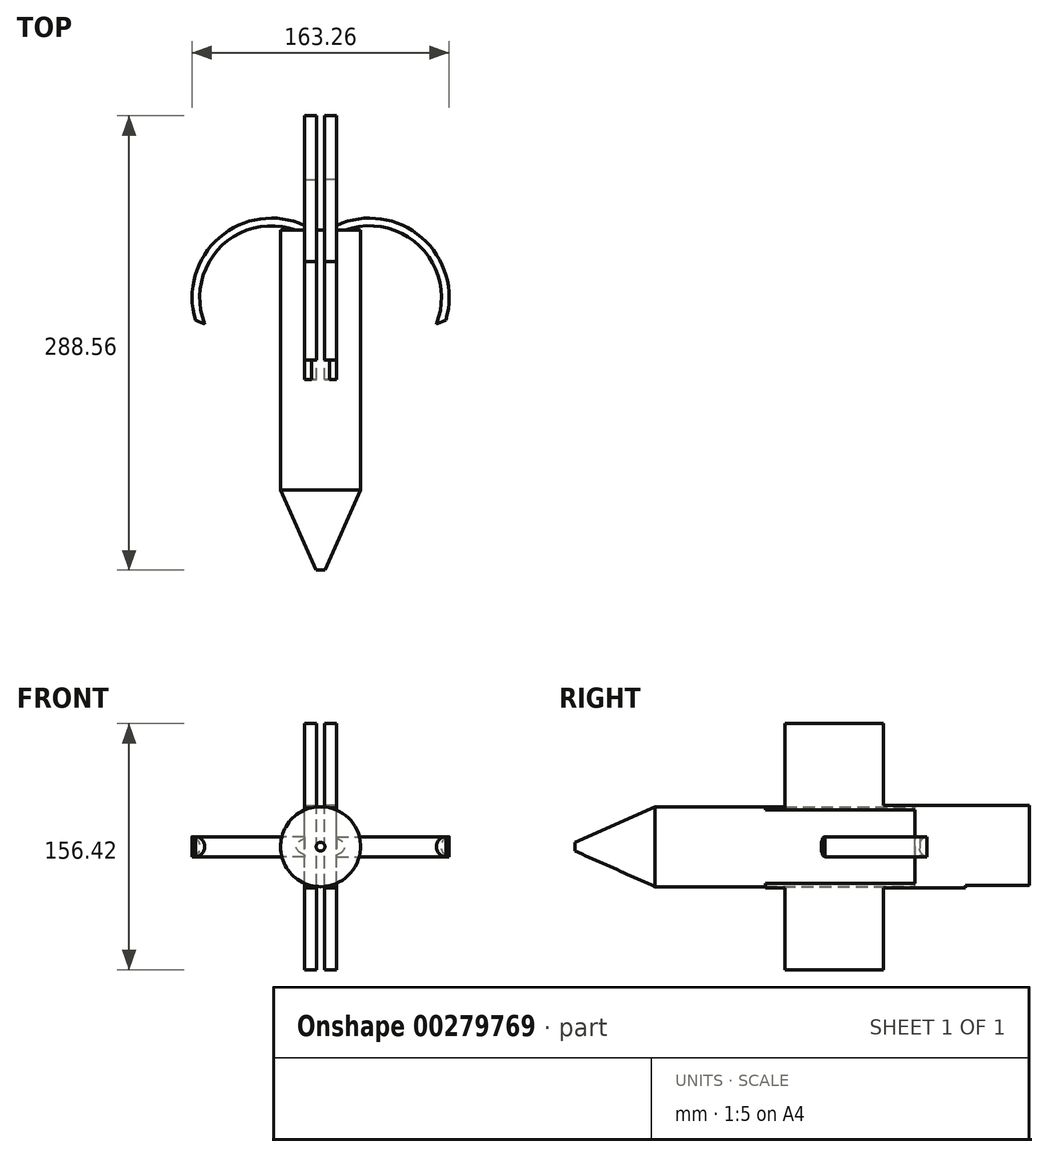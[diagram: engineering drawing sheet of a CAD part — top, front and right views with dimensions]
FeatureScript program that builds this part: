
annotation { "Feature Type Name" : "Feature", "Feature Type Description" : "" }
export const myFeature = defineFeature(function(context is Context, id is Id, definition is map)
    precondition{}
    {
        {
            var Q0;
            Q0=qCreatedBy(makeId("Top.planeOp"),FACE);
            var sketch = newSketch(context, id + "F0", { "sketchPlane" : qUnion([Q0])});
            skLineSegment(sketch, "E0.bottom", {"start": v(-10.87, 76.2) * mm, "end": v(13.75, 76.2) * mm});
            skLineSegment(sketch, "E0.top", {"start": v(-10.87, -76.2) * mm, "end": v(13.75, -76.2) * mm});
            skLineSegment(sketch, "E0.left", {"start": v(-10.87, 76.2) * mm, "end": v(-10.87, -76.2) * mm});
            skLineSegment(sketch, "E0.right", {"start": v(13.75, 76.2) * mm, "end": v(13.75, -76.2) * mm});
            skSolve(sketch);
        }
        {
            var Q0;
            Q0=makeQuery(id+"F0.imprint","IMPRINT",FACE,{"disambiguationData":[TD([[makeQuery(id+"F0.imprint","IMPRINT",EDGE,{"derivedFrom":sQuery(id+"F0.wireOp",EDGE,"E0.bottom")}),-1.0]])]});
            var Q1;
            Q1=sQuery(id+"F0.wireOp",EDGE,"E0.right");
            revolve(context, id + "F1", {"entities" : qUnion([Q0]), "axis" : qUnion([Q1]), "revolveType" : RevolveType.FULL});
        }
        {
            var Q0;
            Q0=makeQuery(id+"F1.opRevolve","SWEPT_BODY",BODY,{"disambiguationData":[OSD([sQuery(id+"F0.wireOp",EDGE,"E0.bottom"),sQuery(id+"F0.wireOp",EDGE,"E0.top"),sQuery(id+"F0.wireOp",EDGE,"E0.left"),sQuery(id+"F0.wireOp",EDGE,"E0.right")])]});
            deleteBodies(context, id + "F2", {"entities" : qUnion([Q0])});
        }
        {
            var Q0;
            Q0=qCreatedBy(makeId("Front.planeOp"),FACE);
            var sketch = newSketch(context, id + "F3", { "sketchPlane" : qUnion([Q0])});
            skCircle(sketch, "E1", {"center": v(0, 0) * mm, "radius": 25.4 * mm});
            skSolve(sketch);
        }
        {
            var Q0;
            Q0=makeQuery(id+"F3.imprint","IMPRINT",FACE,{"disambiguationData":[TD([[makeQuery(id+"F3.imprint","IMPRINT",EDGE,{"derivedFrom":sQuery(id+"F3.wireOp",EDGE,"E1")}),1.0]])]});
            extrude(context, id + "F4", {"entities" : qUnion([Q0]), "endBound" : BoundingType.SYMMETRIC, "depth" : 165.1 * mm});
        }
        {
            var Q0;
            Q0=qCreatedBy(makeId("Right.planeOp"),FACE);
            cPlane(context, id + "F5", {"entities" : qUnion([Q0]), "cplaneType" : CPlaneType.OFFSET, "offset" : 2.54 * mm, "width" : 152.4 * mm, "height" : 152.4 * mm});
        }
        {
            var Q0;
            Q0=makeQuery(id+"F4.opExtrude","CAP_FACE",FACE,{"disambiguationData":[OSD([sQuery(id+"F3.wireOp",EDGE,"E1")])],"isStart":false});
            var sketch = newSketch(context, id + "F6", { "sketchPlane" : qUnion([Q0])});
            skLineSegment(sketch, "E2", {"start": v(0, -2.99) * mm, "end": v(25.36, -1.5) * mm});
            skPoint(sketch, "E3", {"position": v(-28.9, -49.12) * mm});
            skPoint(sketch, "E4", {"position": v(0, -2.99) * mm});
            skPoint(sketch, "E5", {"position": v(-47.51, -18.61) * mm});
            skSolve(sketch);
        }
        {
            var Q0;
            Q0=qCreatedBy(makeId("Right.planeOp"),FACE);
            cPlane(context, id + "F7", {"entities" : qUnion([Q0]), "cplaneType" : CPlaneType.OFFSET, "offset" : 25.4 * mm, "width" : 152.4 * mm, "height" : 152.4 * mm});
        }
        {
            var Q0;
            Q0=qCreatedBy(id+"F5.planeOp",FACE);
            var sketch = newSketch(context, id + "F8", { "sketchPlane" : qUnion([Q0])});
            skLineSegment(sketch, "E6.bottom", {"start": v(0, -74.2) * mm, "end": v(62.5, -74.2) * mm});
            skLineSegment(sketch, "E6.top", {"start": v(0, 78.2) * mm, "end": v(62.5, 78.2) * mm});
            skLineSegment(sketch, "E6.left", {"start": v(0, -74.2) * mm, "end": v(0, 78.2) * mm});
            skLineSegment(sketch, "E6.right", {"start": v(62.5, -74.2) * mm, "end": v(62.5, 78.2) * mm});
            skSolve(sketch);
        }
        {
            var Q0;
            Q0=makeQuery(id+"F8.imprint","IMPRINT",FACE,{"disambiguationData":[TD([[makeQuery(id+"F8.imprint","IMPRINT",EDGE,{"derivedFrom":sQuery(id+"F8.wireOp",EDGE,"E6.bottom")}),1.0]])]});
            extrude(context, id + "F9", {"entities" : qUnion([Q0]), "operationType" : NewBodyOperationType.ADD, "depth" : 7.62 * mm});
        }
        {
            var Q0;
            Q0=makeQuery(id+"F4.opExtrude","SWEPT_BODY",BODY,{"disambiguationData":[OSD([sQuery(id+"F3.wireOp",EDGE,"E1")])]});
            var Q1;
            Q1=qCreatedBy(makeId("Top.planeOp"),FACE);
            mirror(context, id + "F10", {"operationType" : NewBodyOperationType.ADD, "entities" : qUnion([Q0]), "mirrorPlane" : qUnion([Q1])});
        }
        {
            var Q0;
            Q0=qCreatedBy(id+"F5.planeOp",FACE);
            var sketch = newSketch(context, id + "F11", { "sketchPlane" : qUnion([Q0])});
            skLineSegment(sketch, "E7.bottom", {"start": v(-12.47, -26.06) * mm, "end": v(114.53, -26.06) * mm});
            skLineSegment(sketch, "E7.top", {"start": v(-12.47, 24.74) * mm, "end": v(114.53, 24.74) * mm});
            skLineSegment(sketch, "E7.left", {"start": v(-12.47, -26.06) * mm, "end": v(-12.47, 24.74) * mm});
            skLineSegment(sketch, "E7.right", {"start": v(114.53, -26.06) * mm, "end": v(114.53, 24.74) * mm});
            skSolve(sketch);
        }
        {
            var Q0;
            Q0=makeQuery(id+"F11.imprint","IMPRINT",FACE,{"disambiguationData":[TD([[makeQuery(id+"F11.imprint","IMPRINT",EDGE,{"derivedFrom":sQuery(id+"F11.wireOp",EDGE,"E7.bottom")}),1.0]])]});
            extrude(context, id + "F12", {"entities" : qUnion([Q0]), "operationType" : NewBodyOperationType.ADD, "depth" : 7.62 * mm});
        }
        {
            var Q0;
            Q0=qCreatedBy(id+"F5.planeOp",FACE);
            var sketch = newSketch(context, id + "F13", { "sketchPlane" : qUnion([Q0])});
            skLineSegment(sketch, "E8.bottom", {"start": v(2.8, -24.72) * mm, "end": v(155.2, -24.72) * mm});
            skLineSegment(sketch, "E8.top", {"start": v(2.8, 51.48) * mm, "end": v(155.2, 51.48) * mm});
            skLineSegment(sketch, "E8.left", {"start": v(2.8, -24.72) * mm, "end": v(2.8, 51.48) * mm});
            skLineSegment(sketch, "E8.right", {"start": v(155.2, -24.72) * mm, "end": v(155.2, 51.48) * mm});
            skSolve(sketch);
        }
        {
            var Q0;
            Q0=makeQuery(id+"F13.imprint","IMPRINT",FACE,{"disambiguationData":[TD([[makeQuery(id+"F13.imprint","IMPRINT",EDGE,{"derivedFrom":sQuery(id+"F13.wireOp",EDGE,"E8.bottom")}),1.0]])]});
            extrude(context, id + "F14", {"entities" : qUnion([Q0]), "operationType" : NewBodyOperationType.ADD, "depth" : 7.62 * mm});
        }
        {
            var Q0;
            Q0=makeQuery(id+"F6.imprint","IMPRINT",FACE,{"disambiguationData":[TD([[makeQuery(id+"F6.imprint","IMPRINT",EDGE,{"derivedFrom":makeQuery(id+"F4.opExtrude","CAP_EDGE",EDGE,{"disambiguationData":[OSD([sQuery(id+"F3.wireOp",EDGE,"E1")])],"isStart":false})}),1.0]])]});
            var sketch = newSketch(context, id + "F15", { "sketchPlane" : qUnion([Q0])});
            skCircle(sketch, "E9", {"center": v(0, 0) * mm, "radius": 25.4 * mm});
            skSolve(sketch);
        }
        {
            var Q0;
            Q0 = qSketchRegion(id + "F15", true);
            extrude(context, id + "F16", {"entities" : qUnion([Q0]), "operationType" : NewBodyOperationType.ADD, "depth" : 50.8 * mm, "hasDraft" : true, "draftAngle" : 24 * degree, "draftPullDirection" : true});
        }
        {
            var Q0;
            Q0=makeQuery(id+"F14.opExtrude","SWEPT_FACE",FACE,{"disambiguationData":[OSD([sQuery(id+"F13.wireOp",EDGE,"E8.top")])]});
            var Q1;
            {var subQ5=sQuery(id+"F8.wireOp",EDGE,"E6.right");var subQ6=makeQuery(id+"F9.opExtrude","SWEPT_FACE",FACE,{"disambiguationData":[OSD([subQ5])]});var subQ13=sQuery(id+"F11.wireOp",EDGE,"E7.bottom");Q1=makeQuery(id+"F12.boolean.opBoolean","SPLIT",FACE,{"disambiguationData":[TD([subQ6])],"derivedFrom":makeQuery(id+"F12.opExtrude","SWEPT_FACE",FACE,{"disambiguationData":[OSD([subQ13])]})});}
            extrude(context, id + "F17", {"entities" : qUnion([Q0, Q1]), "operationType" : NewBodyOperationType.REMOVE, "oppositeDirection" : true, "depth" : 25.4 * mm});
        }
        {
            var Q0;
            Q0=qCreatedBy(makeId("Top.planeOp"),FACE);
            var sketch = newSketch(context, id + "F18", { "sketchPlane" : qUnion([Q0])});
            skArc(sketch, "E10", {"start": v(0, 0) * mm, "mid": v(-35.08, 80.8) * mm, "end": v(-101.38, 22.8) * mm});
            skArc(sketch, "E11", {"start": v(79.54, 25.34) * mm, "mid": v(15.85, 87.78) * mm, "end": v(0, 0) * mm});
            skSolve(sketch);
        }
        {
            var Q0;
            Q0=qCreatedBy(makeId("Right.planeOp"),FACE);
            var sketch = newSketch(context, id + "F19", { "sketchPlane" : qUnion([Q0])});
            skArc(sketch, "E12", {"start": v(0, 6.35) * mm, "mid": v(6.35, 0) * mm, "end": v(0, -6.35) * mm});
            skLineSegment(sketch, "E13", {"start": v(0, -6.35) * mm, "end": v(0, 6.35) * mm});
            skSolve(sketch);
        }
        {
            var Q0;
            Q0 = qSketchRegion(id + "F19", true);
            var Q1;
            Q1=sQuery(id+"F18.wireOp",EDGE,"E11");
            sweep(context, id + "F20", {"operationType" : NewBodyOperationType.ADD, "profiles" : qUnion([Q0]), "path" : qUnion([Q1])});
        }
        {
            var Q0;
            Q0=makeQuery(id+"F4.opExtrude","SWEPT_BODY",BODY,{"disambiguationData":[OSD([sQuery(id+"F3.wireOp",EDGE,"E1")])]});
            var Q1;
            Q1=qCreatedBy(makeId("Right.planeOp"),FACE);
            mirror(context, id + "F21", {"operationType" : NewBodyOperationType.ADD, "entities" : qUnion([Q0]), "mirrorPlane" : qUnion([Q1])});
        }
    });
